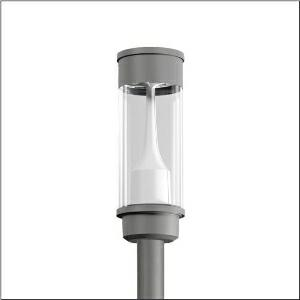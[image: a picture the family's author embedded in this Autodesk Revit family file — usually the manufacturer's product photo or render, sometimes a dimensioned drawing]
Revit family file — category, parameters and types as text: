
# Revit family: litepole_iq___p1_0a_5xa5415ff14hp00022_6790
name_source: partatom
category: Lighting Fixtures
units: mm (PartAtom-declared; Revit-internal decimal feet)

## family parameters
Cut with Voids When Loaded = No
Host = Face
Light Source = No
Part Type = Normal
Room Calculation Point = No
Round Connector Dimension = Use Diameter
Shared = No

## types (1)
- --- (1 x LED, 4700 lm, 33.6 W, 3000K)
    Apparent Load = 34 VA
    CIE Flux Codes = 31 60 90 94 100
    Color Rendering = 70
    Color Temperature = 3000K
    Default Elevation = 1800 mm
    Description = Litepole iQ, mast luminaire, Module 540 iQ-SR, primary light control with 3 zone facetted reflector, of plastic, silver coated, highly specular, structured, primary optical cover: cover, of PMMA, transparent, light distribution: P1.0a, light emission: direct distribution, primary light characteristic: strongly asymmetric, installation type: post-top, LED, High Power LED, rated luminous flux: 4.700lm, luminous efficacy: 140lm/W, light colour: 730, colour temperature: 3000K, control gear: iQ Street-Remote, control: Street-Remote, Auto-Match, Temp-Guard, Lumen-Switch, Night-Set, Smart-Wire, Light-Fading, Desk-Remote (wireless, voltage-free reading and setting of iQ features in the workshop via application-optimized NFC function/RFID function), optimised constant luminous flux control (CLO 2.0), pre-setting: logarithmic dimming characteristic, mains connection: 230..240V, AC, 50/60Hz, connection cable pre-assembled, cable length: 5,5m, wiring characteristics: H07RN-F, start of lifetime: 34W, end of service life: 36W, reduction: 15W, luminaire housing, upper part, of glass-fibre reinforced polyester, coated, Siteco® metallic grey (DB 702S), diameter: 210mm, height: 590mm, spigot size: d x l = 76 x 70mm (post-top) | with reducer (optional accessory) 60 x 70mm, mounting height: 3..5m, post-top mast mounting element, of diecast aluminium, coated, Siteco® metallic grey (DB 702S), Module 540 iQ-SR, traffic white (RAL 9016), equipment: Power, protection rating (complete): IP65, insulation class (complete): insulation class II (safety insulation), certification: CE, ENEC, VDE, packaging unit: 1 piece

Light Distribution: P1.0a
    Height = 590 mm
    Lamp = 1 x LED
    Lamp Light Flux = 4700 lm
    Lamp Power = 33.6 W
    Lamp count = 1
    Length = 220 mm
    Luminous efficacy = 140 lm/W
    Manufacturer = Siteco
    ModVariant = No
    Model = 5XA5415FF14HP00022
    Number of Poles = 1
    OnlyDefault = Yes
    Power Factor = 1
    Product Name = Litepole iQ | P1.0a
    Product group = mast luminaire | pylon top
    ProductGroupID = 6100
    Protection Class = Protection class II
    Protection Degree = IP 65
    RLX_Detail_Level = 1
    RLX_Emergency_Light_Flux = 0 lm
    RLX_Emergency_Type = 0
    RLX_Emergency_Type_DB = No
    RlxData = <blob elided: 29997 chars, md5=6d258500>
    Socket = socket
    Standby Power = 0 W
    System Light Flux = 4700 lm
    System Power = 34 W
    Type Comments = factory setting: luminous flux: 100 % | dim-lin: 254 | 695 mA
    Type Image = l_1006025.jpg
    URL = http://relux.com
    VarID = @adj_216159
    Voltage = 0 V
    Weight = 0.00 kg
    Width = 0 mm  [stored 0 ft]

note: [stored X ft] marks values corroborated as IEEE doubles in the binary element streams (Revit-internal decimal feet)

## geometry (parser evidence)
native form markers: Blend x4, Sweep x11
no freeform markers — native parametric forms only
